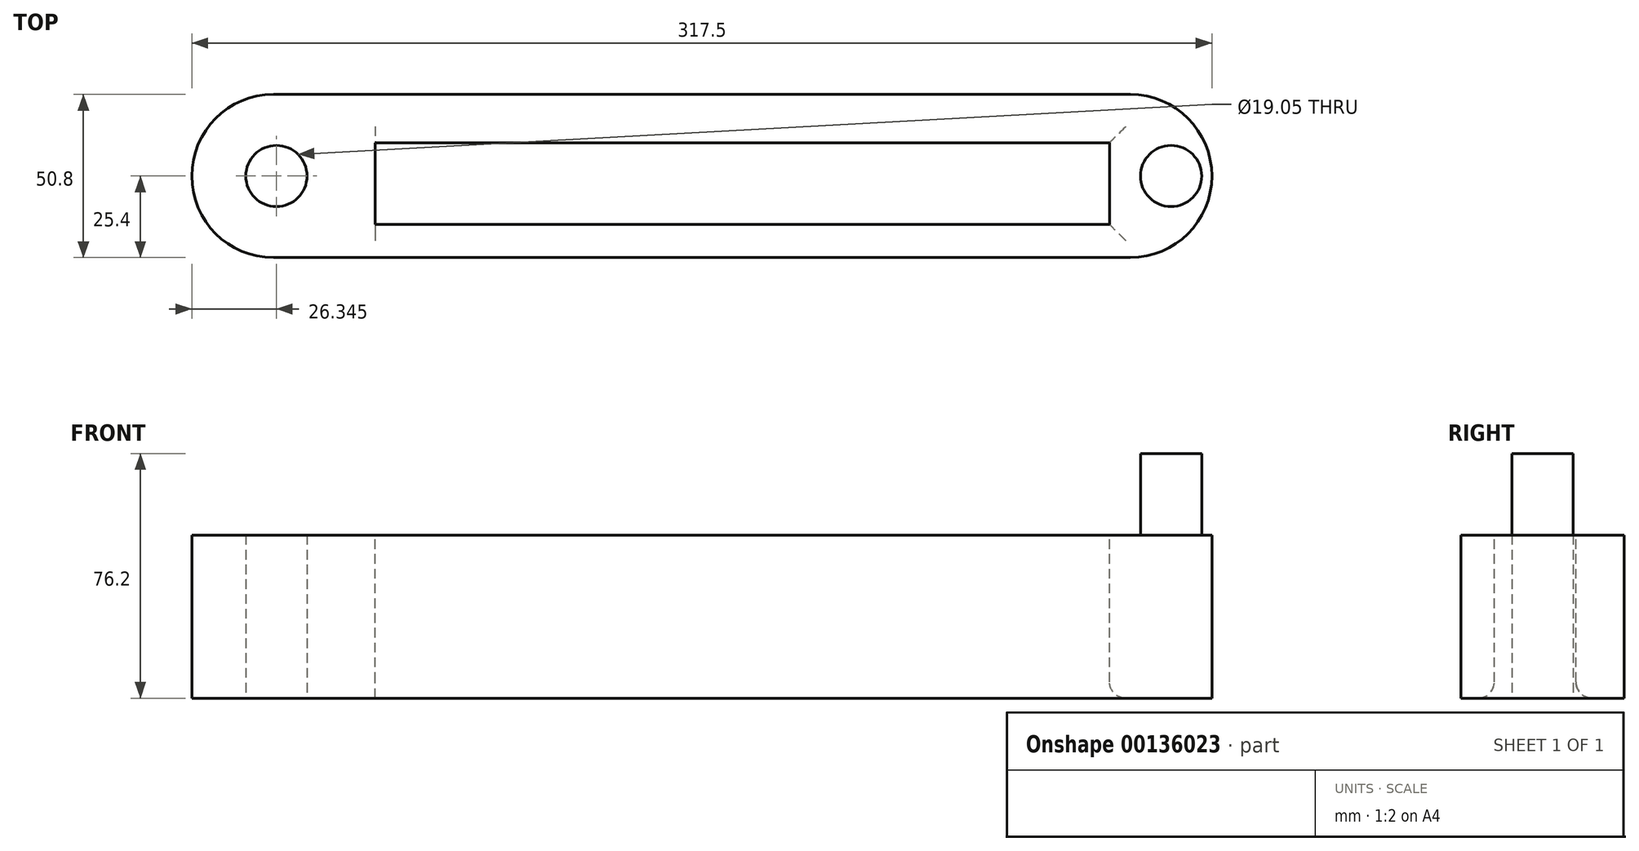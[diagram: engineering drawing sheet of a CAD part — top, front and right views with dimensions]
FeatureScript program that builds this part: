
annotation { "Feature Type Name" : "Feature", "Feature Type Description" : "" }
export const myFeature = defineFeature(function(context is Context, id is Id, definition is map)
    precondition{}
    {
        {
            var Q0;
            Q0=qCreatedBy(makeId("Top.planeOp"),FACE);
            var sketch = newSketch(context, id + "F0", { "sketchPlane" : qUnion([Q0])});
            skLineSegment(sketch, "E0.bottom", {"start": v(0, 0) * mm, "end": v(-317.5, 0) * mm});
            skLineSegment(sketch, "E0.top", {"start": v(0, 50.8) * mm, "end": v(-317.5, 50.8) * mm});
            skLineSegment(sketch, "E0.left", {"start": v(0, 0) * mm, "end": v(0, 50.8) * mm});
            skLineSegment(sketch, "E0.right", {"start": v(-317.5, 0) * mm, "end": v(-317.5, 50.8) * mm});
            skSolve(sketch);
        }
        {
            var Q0;
            Q0=makeQuery(id+"F0.imprint","IMPRINT",FACE,{"disambiguationData":[TD([[makeQuery(id+"F0.imprint","IMPRINT",EDGE,{"derivedFrom":sQuery(id+"F0.wireOp",EDGE,"E0.bottom")}),-1.0]])]});
            extrude(context, id + "F1", {"entities" : qUnion([Q0]), "depth" : 50.8 * mm});
        }
        {
            var Q0;
            Q0=makeQuery(id+"F1.opExtrude","CAP_FACE",FACE,{"disambiguationData":[OSD([sQuery(id+"F0.wireOp",EDGE,"E0.bottom"),sQuery(id+"F0.wireOp",EDGE,"E0.top"),sQuery(id+"F0.wireOp",EDGE,"E0.left"),sQuery(id+"F0.wireOp",EDGE,"E0.right")])],"isStart":false});
            var sketch = newSketch(context, id + "F2", { "sketchPlane" : qUnion([Q0])});
            skSolve(sketch);
        }
        {
            var Q0;
            Q0=makeQuery(id+"F2.imprint","IMPRINT",FACE,{"disambiguationData":[TD([[makeQuery(id+"F2.imprint","IMPRINT",EDGE,{"derivedFrom":makeQuery(id+"F1.opExtrude","CAP_EDGE",EDGE,{"disambiguationData":[OSD([sQuery(id+"F0.wireOp",EDGE,"E0.bottom")])],"isStart":false})}),-1.0]])]});
            var sketch = newSketch(context, id + "F3", { "sketchPlane" : qUnion([Q0])});
            skLineSegment(sketch, "E1.bottom", {"start": v(0, 50.8) * mm, "end": v(-25.4, 50.8) * mm});
            skLineSegment(sketch, "E1.top", {"start": v(0, 0) * mm, "end": v(-25.4, 0) * mm});
            skLineSegment(sketch, "E1.left", {"start": v(0, 50.8) * mm, "end": v(0, 0) * mm});
            skLineSegment(sketch, "E1.right", {"start": v(-25.4, 50.8) * mm, "end": v(-25.4, 0) * mm});
            skCircle(sketch, "E2", {"center": v(-12.7, 25.4) * mm, "radius": 9.53 * mm});
            skSolve(sketch);
        }
        {
            var Q0;
            Q0=makeQuery(id+"F3.imprint","IMPRINT",FACE,{"disambiguationData":[TD([[makeQuery(id+"F3.imprint","IMPRINT",EDGE,{"derivedFrom":sQuery(id+"F3.wireOp",EDGE,"E2")}),1.0]])]});
            extrude(context, id + "F4", {"entities" : qUnion([Q0]), "operationType" : NewBodyOperationType.ADD, "depth" : 25.4 * mm});
        }
        {
            var Q0;
            Q0=makeQuery(id+"F1.opExtrude","CAP_FACE",FACE,{"disambiguationData":[OSD([sQuery(id+"F0.wireOp",EDGE,"E0.bottom"),sQuery(id+"F0.wireOp",EDGE,"E0.top"),sQuery(id+"F0.wireOp",EDGE,"E0.left"),sQuery(id+"F0.wireOp",EDGE,"E0.right")])],"isStart":true});
            var sketch = newSketch(context, id + "F5", { "sketchPlane" : qUnion([Q0])});
            skLineSegment(sketch, "E3.bottom", {"start": v(-274.12, -27.37) * mm, "end": v(-248.72, -27.37) * mm});
            skLineSegment(sketch, "E3.top", {"start": v(-274.12, 0) * mm, "end": v(-248.72, 0) * mm});
            skLineSegment(sketch, "E3.left", {"start": v(-274.12, -27.37) * mm, "end": v(-274.12, 0) * mm});
            skLineSegment(sketch, "E3.right", {"start": v(-248.72, -27.37) * mm, "end": v(-248.72, 0) * mm});
            skPoint(sketch, "E4", {"position": v(-291.16, -25.4) * mm});
            skPoint(sketch, "E4.positionSnap0", {"position": v(-317.5, -25.4) * mm});
            skSolve(sketch);
        }
        {
            var Q0;
            Q0=sQuery(id+"F5.wireOp",VERTEX,"E4");
            var Q1;
            Q1=makeQuery(id+"F1.opExtrude","SWEPT_BODY",BODY,{"disambiguationData":[OSD([sQuery(id+"F0.wireOp",EDGE,"E0.bottom"),sQuery(id+"F0.wireOp",EDGE,"E0.top"),sQuery(id+"F0.wireOp",EDGE,"E0.left"),sQuery(id+"F0.wireOp",EDGE,"E0.right")])]});
            hole(context, id + "F6", {"style" : HoleStyle.C_SINK, "endStyle" : HoleEndStyle.THROUGH, "holeDiameter" : 19.05 * mm, "cSinkDiameter" : 19.05 * mm, "cSinkAngle" : 90 * degree, "locations" : qUnion([Q0]), "scope" : qUnion([Q1]), "isTappedThrough" : true});
        }
        {
            var Q0;
            Q0=makeQuery(id+"F1.opExtrude","SWEPT_EDGE",EDGE,{"disambiguationData":[OSD([sQuery(id+"F0.wireOp",EDGE,"E0.top"),sQuery(id+"F0.wireOp",EDGE,"E0.left")])]});
            var Q1;
            Q1=makeQuery(id+"F1.opExtrude","SWEPT_EDGE",EDGE,{"disambiguationData":[OSD([sQuery(id+"F0.wireOp",EDGE,"E0.bottom"),sQuery(id+"F0.wireOp",EDGE,"E0.left")])]});
            var Q2;
            Q2=makeQuery(id+"F1.opExtrude","SWEPT_EDGE",EDGE,{"disambiguationData":[OSD([sQuery(id+"F0.wireOp",EDGE,"E0.top"),sQuery(id+"F0.wireOp",EDGE,"E0.right")])]});
            var Q3;
            Q3=makeQuery(id+"F1.opExtrude","SWEPT_EDGE",EDGE,{"disambiguationData":[OSD([sQuery(id+"F0.wireOp",EDGE,"E0.bottom"),sQuery(id+"F0.wireOp",EDGE,"E0.right")])]});
            fillet(context, id + "F7", {"entities" : qUnion([Q0, Q1, Q2, Q3]), "radius" : 25.4 * mm, "tangentPropagation" : true, "allowEdgeOverflow" : false});
        }
        {
            var Q0;
            Q0=makeQuery(id+"F2.imprint","IMPRINT",FACE,{"disambiguationData":[TD([[makeQuery(id+"F2.imprint","IMPRINT",EDGE,{"derivedFrom":makeQuery(id+"F1.opExtrude","CAP_EDGE",EDGE,{"disambiguationData":[OSD([sQuery(id+"F0.wireOp",EDGE,"E0.bottom")])],"isStart":false})}),-1.0]])]});
            var sketch = newSketch(context, id + "F8", { "sketchPlane" : qUnion([Q0])});
            skLineSegment(sketch, "E5", {"start": v(-260.46, 35.76) * mm, "end": v(-260.46, 0) * mm});
            skPoint(sketch, "E6", {"position": v(-260.46, 23.06) * mm});
            skLineSegment(sketch, "E7.bottom", {"start": v(-260.46, 23.06) * mm, "end": v(-31.86, 23.06) * mm});
            skLineSegment(sketch, "E7.top", {"start": v(-260.46, 35.76) * mm, "end": v(-31.86, 35.76) * mm});
            skLineSegment(sketch, "E7.left", {"start": v(-260.46, 23.06) * mm, "end": v(-260.46, 35.76) * mm});
            skLineSegment(sketch, "E7.right", {"start": v(-31.86, 23.06) * mm, "end": v(-31.86, 35.76) * mm});
            skPoint(sketch, "E8.orphan", {"position": v(-260.46, 46.11) * mm});
            skLineSegment(sketch, "E9", {"start": v(-260.46, 0) * mm, "end": v(-260.46, 46.11) * mm});
            skLineSegment(sketch, "E10.top", {"start": v(-260.46, 10.36) * mm, "end": v(-31.86, 10.36) * mm});
            skLineSegment(sketch, "E10.left", {"start": v(-260.46, 23.06) * mm, "end": v(-260.46, 10.36) * mm});
            skLineSegment(sketch, "E10.right", {"start": v(-31.86, 23.06) * mm, "end": v(-31.86, 10.36) * mm});
            skSolve(sketch);
        }
        {
            var Q0;
            {var subQ0=sQuery(id+"F8.wireOp",EDGE,"E7.top");Q0=makeQuery(id+"F8.imprint","IMPRINT",FACE,{"disambiguationData":[TD([[makeQuery(id+"F8.imprint","IMPRINT",EDGE,{"derivedFrom":subQ0}),-1.0]])]});}
            var Q1;
            Q1=makeQuery(id+"F8.imprint","IMPRINT",FACE,{"disambiguationData":[TD([[makeQuery(id+"F8.imprint","IMPRINT",EDGE,{"derivedFrom":sQuery(id+"F8.wireOp",EDGE,"E7.bottom")}),-1.0]])]});
            extrude(context, id + "F9", {"entities" : qUnion([Q0, Q1]), "operationType" : NewBodyOperationType.REMOVE, "oppositeDirection" : true, "depth" : 127 * mm});
        }
        {
            var Q0;
            Q0=makeQuery(id+"F9.boolean.opBoolean","COPY",EDGE,{"derivedFrom":makeQuery(id+"F9.opExtrude","CAP_EDGE",EDGE,{"disambiguationData":[OSD([sQuery(id+"F8.wireOp",EDGE,"E7.right"),sQuery(id+"F8.wireOp",EDGE,"E10.right")])],"isStart":true})});
            var Q1;
            Q1=makeQuery(id+"F9.boolean.opBoolean","INTERSECT",EDGE,{"derivedFrom":[makeQuery(id+"F1.opExtrude","CAP_FACE",FACE,{"disambiguationData":[OSD([sQuery(id+"F0.wireOp",EDGE,"E0.bottom"),sQuery(id+"F0.wireOp",EDGE,"E0.top"),sQuery(id+"F0.wireOp",EDGE,"E0.left"),sQuery(id+"F0.wireOp",EDGE,"E0.right")])],"isStart":true}),makeQuery(id+"F9.opExtrude","SWEPT_FACE",FACE,{"disambiguationData":[OSD([sQuery(id+"F8.wireOp",EDGE,"E7.right"),sQuery(id+"F8.wireOp",EDGE,"E10.right")])]})]});
            var Q2;
            Q2=makeQuery(id+"F9.boolean.opBoolean","COPY",EDGE,{"derivedFrom":makeQuery(id+"F9.opExtrude","CAP_EDGE",EDGE,{"disambiguationData":[OSD([sQuery(id+"F8.wireOp",EDGE,"E10.top")])],"isStart":true})});
            var Q3;
            Q3=makeQuery(id+"F9.boolean.opBoolean","COPY",EDGE,{"derivedFrom":makeQuery(id+"F9.opExtrude","CAP_EDGE",EDGE,{"disambiguationData":[OSD([sQuery(id+"F8.wireOp",EDGE,"E9"),sQuery(id+"F8.wireOp",EDGE,"E10.left")])],"isStart":true})});
            var Q4;
            Q4=makeQuery(id+"F9.boolean.opBoolean","COPY",EDGE,{"derivedFrom":makeQuery(id+"F9.opExtrude","CAP_EDGE",EDGE,{"disambiguationData":[OSD([sQuery(id+"F8.wireOp",EDGE,"E7.top")])],"isStart":true})});
            var Q5;
            Q5=makeQuery(id+"F9.boolean.opBoolean","INTERSECT",EDGE,{"derivedFrom":[makeQuery(id+"F1.opExtrude","CAP_FACE",FACE,{"disambiguationData":[OSD([sQuery(id+"F0.wireOp",EDGE,"E0.bottom"),sQuery(id+"F0.wireOp",EDGE,"E0.top"),sQuery(id+"F0.wireOp",EDGE,"E0.left"),sQuery(id+"F0.wireOp",EDGE,"E0.right")])],"isStart":true}),makeQuery(id+"F9.opExtrude","SWEPT_FACE",FACE,{"disambiguationData":[OSD([sQuery(id+"F8.wireOp",EDGE,"E10.top")])]})]});
            var Q6;
            Q6=makeQuery(id+"F9.boolean.opBoolean","INTERSECT",EDGE,{"derivedFrom":[makeQuery(id+"F1.opExtrude","CAP_FACE",FACE,{"disambiguationData":[OSD([sQuery(id+"F0.wireOp",EDGE,"E0.bottom"),sQuery(id+"F0.wireOp",EDGE,"E0.top"),sQuery(id+"F0.wireOp",EDGE,"E0.left"),sQuery(id+"F0.wireOp",EDGE,"E0.right")])],"isStart":true}),makeQuery(id+"F9.opExtrude","SWEPT_FACE",FACE,{"disambiguationData":[OSD([sQuery(id+"F8.wireOp",EDGE,"E7.top")])]})]});
            var Q7;
            Q7=makeQuery(id+"F9.boolean.opBoolean","INTERSECT",EDGE,{"derivedFrom":[makeQuery(id+"F1.opExtrude","CAP_FACE",FACE,{"disambiguationData":[OSD([sQuery(id+"F0.wireOp",EDGE,"E0.bottom"),sQuery(id+"F0.wireOp",EDGE,"E0.top"),sQuery(id+"F0.wireOp",EDGE,"E0.left"),sQuery(id+"F0.wireOp",EDGE,"E0.right")])],"isStart":true}),makeQuery(id+"F9.opExtrude","SWEPT_FACE",FACE,{"disambiguationData":[OSD([sQuery(id+"F8.wireOp",EDGE,"E9"),sQuery(id+"F8.wireOp",EDGE,"E10.left")])]})]});
            fillet(context, id + "F10", {"entities" : qUnion([Q0, Q1, Q2, Q3, Q4, Q5, Q6, Q7]), "radius" : 5.08 * mm, "tangentPropagation" : true, "allowEdgeOverflow" : false});
        }
    });
